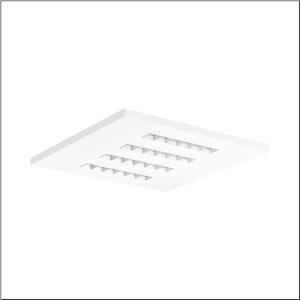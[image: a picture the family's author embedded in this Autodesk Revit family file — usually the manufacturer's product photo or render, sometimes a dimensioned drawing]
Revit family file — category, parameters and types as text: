
# Revit family: silica_r__21_square_51mx6mds34w_a914
name_source: partatom
category: Lighting Fixtures
units: mm (PartAtom-declared; Revit-internal decimal feet)

## family parameters
Cut with Voids When Loaded = No
Host = Face
Light Source = No
Part Type = Normal
Room Calculation Point = No
Round Connector Dimension = Use Diameter
Shared = No

## types (1)
- --- (1 x LED, 4600 lm, 29.2 W, 3000K)
    Apparent Load = 29 VA
    CIE Flux Codes = 83 98 100 100 100
    Color Rendering = 80
    Color Temperature = 3000K
    Default Elevation = 1800 mm
    Description = Silica® 21 Square, office luminaire, primary light control with lens, of PMMA, primary anti-glare with reflector, of PC, white, CAT 2 (L<= 3000cd/m²), light emission: direct distribution, primary light characteristic: symmetric, installation type: lay-in mounting, LED, rated luminous flux: 4.600lm, luminous efficacy: 158lm/W, light colour: 830, colour temperature: 3000K, with terminal, 5-pole, mains connection: 220..240V, AC, 50/60Hz, rated input power: 29.2W, luminaire housing, of sheet steel, coated, traffic white (RAL 9016), module: M600, length: 597mm, width: 597mm, height: 33mm, protection rating (complete): IP20, insulation class (complete): insulation class I (protective earthing), certification: CE, permissible operating ambient temperature: -20..+40°C, standard: EN 50419, packaging unit: 1 piece
    Height = 0 mm  [stored 0 ft]
    Lamp = 1 x LED
    Lamp Light Flux = 4600 lm
    Lamp Power = 29.2 W
    Lamp count = 1
    Length = 597 mm
    Luminous efficacy = 158 lm/W
    Manufacturer = Siteco
    ModVariant = No
    Model = 51MX6MDS34W
    Mounting Place = Ceiling
    Mounting Type = Recessed
    Number of Poles = 1
    OnlyDefault = Yes
    Power Factor = 1
    Product Name = Silica® 21 Square
    Product group = office luminaire | ceiling recessed
    ProductGroupID = 401
    Protection Class = Protection class I
    Protection Degree = IP 20
    RLX_Detail_Level = 1
    RLX_Emergency_Light_Flux = 0 lm
    RLX_Emergency_Type = 0
    RLX_Emergency_Type_DB = No
    RlxData = <blob elided: 18505 chars, md5=905ad0ac>
    Socket = socket
    Standby Power = 0 W
    System Light Flux = 4600 lm
    System Power = 29 W
    Type Comments = factory setting: luminous flux: 100 % | dim-lin: 254 | 393 mA
    Type Image = l_1275220.jpg
    URL = http://relux.com
    VarID = @adj_036133
    Voltage = 0 V
    Weight = 0.00 kg
    Width = 597 mm

note: [stored X ft] marks values corroborated as IEEE doubles in the binary element streams (Revit-internal decimal feet)

## geometry (parser evidence)
native form markers: Blend x4, Sweep x12
no freeform markers — native parametric forms only
